# Revit family: SGB-R-LSCS
name_source: partatom
category: Lighting Fixtures
units: mm (PartAtom-declared; Revit-internal decimal feet)

## family parameters
Cut with Voids When Loaded = No
Host = Face
Light Source = Yes
OmniClass Number = 23.80.70.11.14.17
OmniClass Title = Direct/Indirect
Part Type = Normal
Room Calculation Point = No
Round Connector Dimension = Use Diameter
Shared = Yes

## types (1)
- SGB-R-LSCS
    Additional Material Finish = Paint - Matte White
    Apparent Load = 22 W
    Assembly Code = D5020200
    Available Finish Options = Available in Dark bronze finish
    Certifications = Listed to UL1598 for use in wet locations, FCC Title 47 Part 1, IP65
    Color Filter = 16777215
    Color Rendering Index = 80 CRI
    Default Elevation = 48 "
    Description = Sling Round and Square Bollards featuring switchable wattage (12W, 16W, 22W) and CCT (3K, 4K, 5K). Low glare acrylic lens provides uniform distribution in a rugged die-cast aluminium housing.
    Dimming Lamp Color Temperature Shift = <None>
    Distribution Patterns = None
    Emit Shape Visible in Rendering = No
    Emit from Circle Diameter = 5.5 "
    Features = Commercial grade LED Bollard for use in outdoor applications such a commercial building, retail, government and educational facilities 
CCT Selectable: 3000K, 4000K or 5000K
Wattage Selectable: 12W, 16W or 22W 
6" Round or 6" Square with dark bronze finish
    Housing Material = Metal - Dark Bronze
    Installation and Service URL = https://cdn.currentlighting.com
    Lamp = LED
    Lens Material Finish = White Glass
    Load Classification = Lighting
    Manufacturer = Current Lighting
    Model = Sling Bollard SGB-R-LSCS
    Mounting = Please Refer to the Product Spec Sheet for Mounting Options
    No of Poles = 1
    Photometric Web File = SGB-R-LSCS-22W-5K8.ies
    Photometric Web Link = https://www.currentlighting.com
    Photometry Note = Please load ies file listed under Photometric Web File for accurate rendering.
    Power Factor = 0.9
    Product Documentation Link = https://cdn.currentlighting.com
    Product Page URL = https://www.currentlighting.com
    Tilt Angle = 90.00°
    Type Comments = Bollard Light Fixture
    URL = www.currentlighting.com
    Version = 2021 V 1.2
    Voltage = 120 V
    Voltage Comments = Universal Voltage 120V-277V
    Warranty = 5 year limited
    Wattage Comments = 12.1 - 22.3 W

## geometry (parser evidence)
native form markers: Sweep x3
no freeform markers — native parametric forms only
